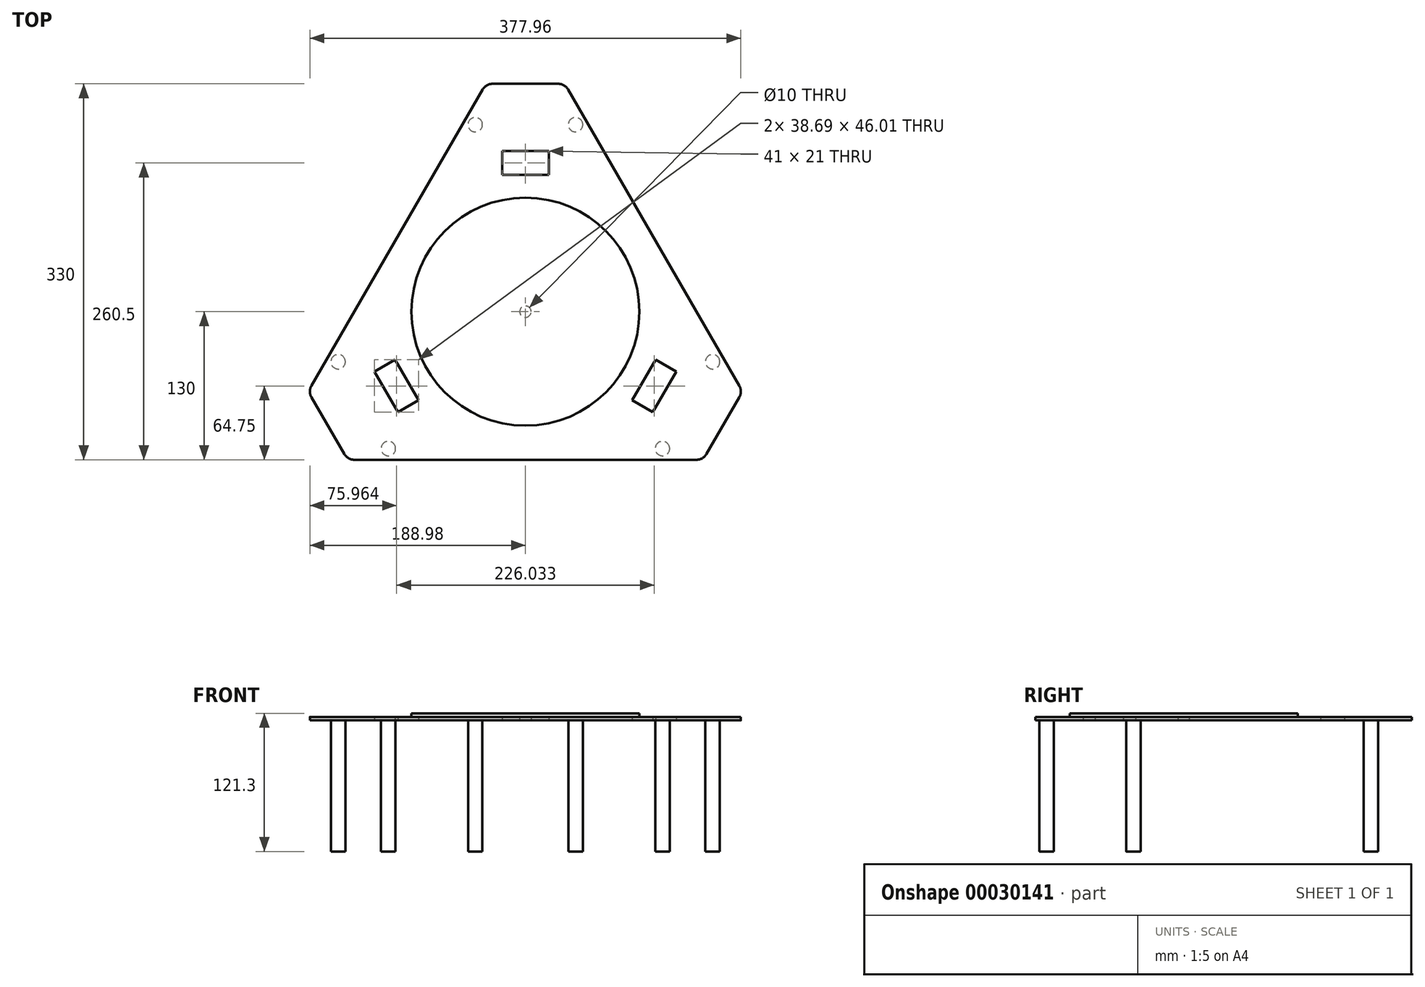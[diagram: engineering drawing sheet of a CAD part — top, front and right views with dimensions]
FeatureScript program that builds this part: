
annotation { "Feature Type Name" : "Feature", "Feature Type Description" : "" }
export const myFeature = defineFeature(function(context is Context, id is Id, definition is map)
    precondition{}
    {
        {
            var Q0;
            Q0=qCreatedBy(makeId("Top.planeOp"),FACE);
            var sketch = newSketch(context, id + "F0", { "sketchPlane" : qUnion([Q0])});
            skCircle(sketch, "E0", {"center": v(0, 0) * mm, "radius": 100 * mm, "construction": true});
            skLineSegment(sketch, "E1", {"start": v(0, 200) * mm, "end": v(-173.2, -100) * mm, "construction": true});
            skLineSegment(sketch, "E2", {"start": v(-173.2, -100) * mm, "end": v(173.2, -100) * mm, "construction": true});
            skLineSegment(sketch, "E3", {"start": v(173.2, -100) * mm, "end": v(0, 200) * mm, "construction": true});
            skLineSegment(sketch, "E4.0", {"start": v(190.53, -70) * mm, "end": v(34.64, 200) * mm});
            skLineSegment(sketch, "E4.1", {"start": v(-155.88, -130) * mm, "end": v(155.88, -130) * mm});
            skLineSegment(sketch, "E4.2", {"start": v(-34.64, 200) * mm, "end": v(-190.53, -70) * mm});
            skLineSegment(sketch, "E5", {"start": v(155.88, -130) * mm, "end": v(190.53, -70) * mm});
            skLineSegment(sketch, "E6", {"start": v(-190.53, -70) * mm, "end": v(-155.88, -130) * mm});
            skLineSegment(sketch, "E7", {"start": v(-34.64, 200) * mm, "end": v(34.64, 200) * mm});
            skCircle(sketch, "E8", {"center": v(0, 0) * mm, "radius": 5 * mm});
            skLineSegment(sketch, "E9", {"start": v(0, 0) * mm, "end": v(173.2, -100) * mm, "construction": true});
            skLineSegment(sketch, "E10", {"start": v(-173.2, -100) * mm, "end": v(-173.2, -100) * mm});
            skLineSegment(sketch, "E11", {"start": v(0, 0) * mm, "end": v(-173.2, -100) * mm, "construction": true});
            skLineSegment(sketch, "E12", {"start": v(0, 0) * mm, "end": v(0, 200) * mm, "construction": true});
            skLineSegment(sketch, "E13", {"start": v(-132.36, -52.75) * mm, "end": v(-111.86, -88.25) * mm});
            skLineSegment(sketch, "E14", {"start": v(-111.86, -88.25) * mm, "end": v(-93.67, -77.75) * mm});
            skLineSegment(sketch, "E15", {"start": v(-132.36, -52.75) * mm, "end": v(-114.17, -42.25) * mm});
            skLineSegment(sketch, "E16", {"start": v(-114.17, -42.25) * mm, "end": v(-93.67, -77.75) * mm});
            skPoint(sketch, "E17", {"position": v(-122.1, -70.5) * mm});
            skSolve(sketch);
        }
        {
            var Q0;
            Q0 = qSketchRegion(id + "F0", true);
            var Q1;
            Q1=makeQuery(id+"F0.imprint","IMPRINT",FACE,{"disambiguationData":[TD([[makeQuery(id+"F0.imprint","IMPRINT",EDGE,{"derivedFrom":sQuery(id+"F0.wireOp",EDGE,"E4.0")}),1.0]])]});
            extrude(context, id + "F7", {"entities" : qUnion([Q0, Q1]), "depth" : 3 * mm});
        }
        {
            var Q0;
            Q0=makeQuery(id+"F7.opExtrude","SWEPT_FACE",FACE,{"disambiguationData":[OSD([sQuery(id+"F0.wireOp",EDGE,"E16")])]});
            var Q1;
            Q1=makeQuery(id+"F7.opExtrude","SWEPT_FACE",FACE,{"disambiguationData":[OSD([sQuery(id+"F0.wireOp",EDGE,"E14")])]});
            var Q2;
            Q2=makeQuery(id+"F7.opExtrude","SWEPT_FACE",FACE,{"disambiguationData":[OSD([sQuery(id+"F0.wireOp",EDGE,"E13")])]});
            var Q3;
            Q3=makeQuery(id+"F7.opExtrude","SWEPT_FACE",FACE,{"disambiguationData":[OSD([sQuery(id+"F0.wireOp",EDGE,"E15")])]});
            var Q4;
            Q4=makeQuery(id+"F7.opExtrude","SWEPT_FACE",FACE,{"disambiguationData":[OSD([sQuery(id+"F0.wireOp",EDGE,"E8")])]});
            circularPattern(context, id + "F8", {"operationType" : NewBodyOperationType.REMOVE, "faces" : qUnion([Q0, Q1, Q2, Q3]), "axis" : qUnion([Q4]), "angle" : 120 * degree, "instanceCount" : 3, "patternType" : PatternType.FACE});
        }
        {
            var Q0;
            Q0=makeQuery(id+"F7.opExtrude","CAP_FACE",FACE,{"disambiguationData":[OSD([sQuery(id+"F0.wireOp",EDGE,"E4.0"),sQuery(id+"F0.wireOp",EDGE,"E4.1"),sQuery(id+"F0.wireOp",EDGE,"E4.2"),sQuery(id+"F0.wireOp",EDGE,"E5"),sQuery(id+"F0.wireOp",EDGE,"E6"),sQuery(id+"F0.wireOp",EDGE,"E7"),sQuery(id+"F0.wireOp",EDGE,"E8"),sQuery(id+"F0.wireOp",EDGE,"E13"),sQuery(id+"F0.wireOp",EDGE,"E14"),sQuery(id+"F0.wireOp",EDGE,"E15"),sQuery(id+"F0.wireOp",EDGE,"E16")])],"isStart":false});
            var sketch = newSketch(context, id + "F1", { "sketchPlane" : qUnion([Q0])});
            skCircle(sketch, "E18", {"center": v(0, 0) * mm, "radius": 100 * mm});
            skSolve(sketch);
        }
        {
            var Q0;
            Q0 = qSketchRegion(id + "F1", true);
            extrude(context, id + "F2", {"entities" : qUnion([Q0]), "depth" : 3.3 * mm});
        }
        {
            var Q0;
            Q0=makeQuery(id+"F7.opExtrude","SWEPT_EDGE",EDGE,{"disambiguationData":[OSD([sQuery(id+"F0.wireOp",EDGE,"E4.1"),sQuery(id+"F0.wireOp",EDGE,"E6")])]});
            var Q1;
            Q1=makeQuery(id+"F7.opExtrude","SWEPT_EDGE",EDGE,{"disambiguationData":[OSD([sQuery(id+"F0.wireOp",EDGE,"E4.2"),sQuery(id+"F0.wireOp",EDGE,"E6")])]});
            var Q2;
            Q2=makeQuery(id+"F7.opExtrude","SWEPT_EDGE",EDGE,{"disambiguationData":[OSD([sQuery(id+"F0.wireOp",EDGE,"E4.1"),sQuery(id+"F0.wireOp",EDGE,"E5")])]});
            var Q3;
            Q3=makeQuery(id+"F7.opExtrude","SWEPT_EDGE",EDGE,{"disambiguationData":[OSD([sQuery(id+"F0.wireOp",EDGE,"E4.0"),sQuery(id+"F0.wireOp",EDGE,"E5")])]});
            var Q4;
            Q4=makeQuery(id+"F7.opExtrude","SWEPT_EDGE",EDGE,{"disambiguationData":[OSD([sQuery(id+"F0.wireOp",EDGE,"E4.0"),sQuery(id+"F0.wireOp",EDGE,"E7")])]});
            var Q5;
            Q5=makeQuery(id+"F7.opExtrude","SWEPT_EDGE",EDGE,{"disambiguationData":[OSD([sQuery(id+"F0.wireOp",EDGE,"E4.2"),sQuery(id+"F0.wireOp",EDGE,"E7")])]});
            fillet(context, id + "F3", {"entities" : qUnion([Q0, Q1, Q2, Q3, Q4, Q5]), "radius" : 10 * mm, "tangentPropagation" : true, "allowEdgeOverflow" : false});
        }
        {
            var Q0;
            Q0=makeQuery(id+"F7.opExtrude","CAP_FACE",FACE,{"disambiguationData":[OSD([sQuery(id+"F0.wireOp",EDGE,"E4.0"),sQuery(id+"F0.wireOp",EDGE,"E4.1"),sQuery(id+"F0.wireOp",EDGE,"E4.2"),sQuery(id+"F0.wireOp",EDGE,"E5"),sQuery(id+"F0.wireOp",EDGE,"E6"),sQuery(id+"F0.wireOp",EDGE,"E7"),sQuery(id+"F0.wireOp",EDGE,"E8"),sQuery(id+"F0.wireOp",EDGE,"E13"),sQuery(id+"F0.wireOp",EDGE,"E14"),sQuery(id+"F0.wireOp",EDGE,"E15"),sQuery(id+"F0.wireOp",EDGE,"E16")])],"isStart":true});
            var sketch = newSketch(context, id + "F4", { "sketchPlane" : qUnion([Q0])});
            skCircle(sketch, "E19", {"center": v(-120.2, 120.2) * mm, "radius": 6.35 * mm});
            skPoint(sketch, "E20", {"position": v(0, 0) * mm});
            skLineSegment(sketch, "E21", {"start": v(-120.2, 120.2) * mm, "end": v(0, 0) * mm, "construction": true});
            skLineSegment(sketch, "E22", {"start": v(0, 0) * mm, "end": v(0, 130) * mm, "construction": true});
            skLineSegment(sketch, "E23", {"start": v(0, 0) * mm, "end": v(-164.2, 44) * mm, "construction": true});
            skCircle(sketch, "E24", {"center": v(-164.2, 44) * mm, "radius": 6.35 * mm});
            skSolve(sketch);
        }
        {
            var Q0;
            Q0=makeQuery(id+"F4.imprint","IMPRINT",FACE,{"disambiguationData":[TD([[makeQuery(id+"F4.imprint","IMPRINT",EDGE,{"derivedFrom":sQuery(id+"F4.wireOp",EDGE,"E19")}),1.0]])]});
            var Q1;
            Q1=makeQuery(id+"F4.imprint","IMPRINT",FACE,{"disambiguationData":[TD([[makeQuery(id+"F4.imprint","IMPRINT",EDGE,{"derivedFrom":sQuery(id+"F4.wireOp",EDGE,"E24")}),1.0]])]});
            extrude(context, id + "F5", {"entities" : qUnion([Q0, Q1]), "depth" : 115 * mm});
        }
        {
            var Q0;
            Q0=makeQuery(id+"F5.opExtrude","SWEPT_BODY",BODY,{"disambiguationData":[OSD([sQuery(id+"F4.wireOp",EDGE,"E19")])]});
            var Q1;
            Q1=makeQuery(id+"F5.opExtrude","SWEPT_BODY",BODY,{"disambiguationData":[OSD([sQuery(id+"F4.wireOp",EDGE,"E24")])]});
            var Q2;
            Q2=makeQuery(id+"F7.opExtrude","CAP_EDGE",EDGE,{"disambiguationData":[OSD([sQuery(id+"F0.wireOp",EDGE,"E8")])],"isStart":true});
            circularPattern(context, id + "F6", {"entities" : qUnion([Q0, Q1]), "axis" : qUnion([Q2]), "angle" : 360 * degree, "instanceCount" : 3, "equalSpace" : true});
        }
    });
